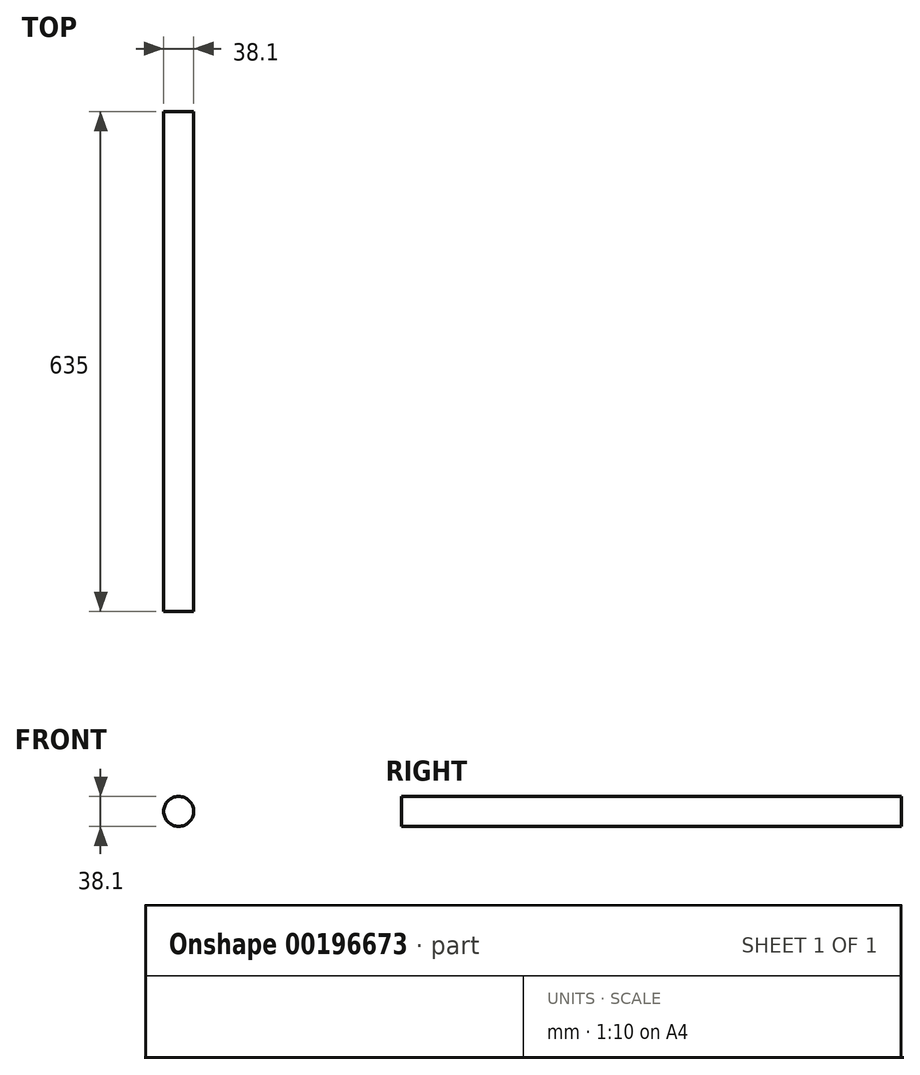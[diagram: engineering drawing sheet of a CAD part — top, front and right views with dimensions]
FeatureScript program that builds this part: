
annotation { "Feature Type Name" : "Feature", "Feature Type Description" : "" }
export const myFeature = defineFeature(function(context is Context, id is Id, definition is map)
    precondition{}
    {
        {
            var Q0;
            Q0=qCreatedBy(makeId("Front.planeOp"),FACE);
            var sketch = newSketch(context, id + "F0", { "sketchPlane" : qUnion([Q0])});
            skCircle(sketch, "E0", {"center": v(0, 0) * mm, "radius": 19.05 * mm});
            skSolve(sketch);
        }
        {
            var Q0;
            Q0=makeQuery(id+"F0.imprint","IMPRINT",FACE,{"disambiguationData":[TD([[makeQuery(id+"F0.imprint","IMPRINT",EDGE,{"derivedFrom":sQuery(id+"F0.wireOp",EDGE,"E0")}),1.0]])]});
            extrude(context, id + "F1", {"entities" : qUnion([Q0]), "depth" : 635 * mm});
        }
    });
